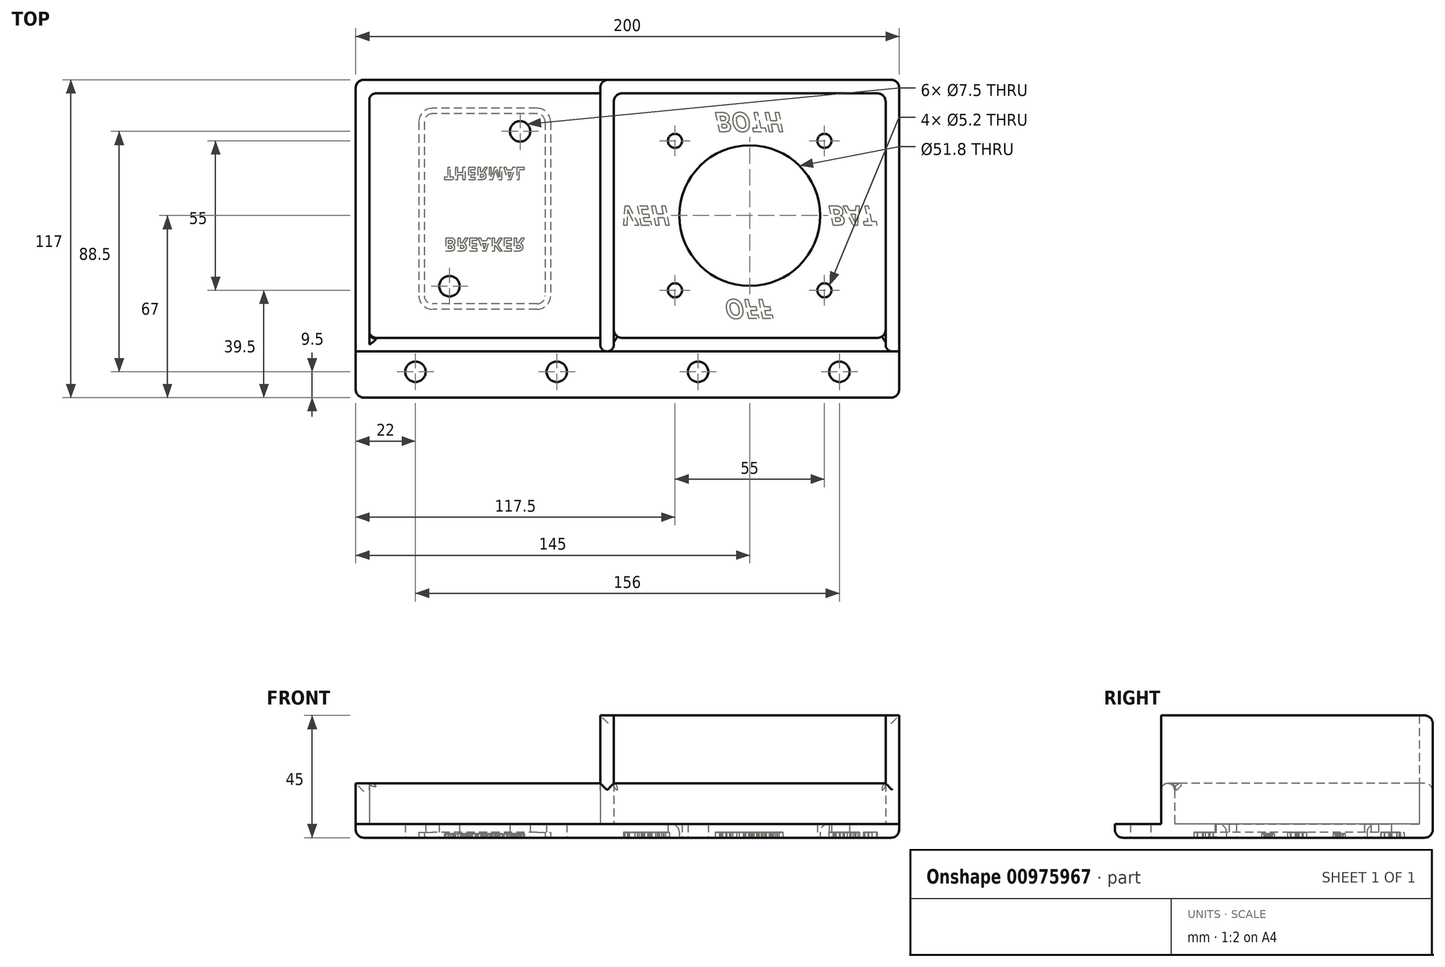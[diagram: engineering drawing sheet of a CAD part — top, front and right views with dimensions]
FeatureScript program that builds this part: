
annotation { "Feature Type Name" : "Feature", "Feature Type Description" : "" }
export const myFeature = defineFeature(function(context is Context, id is Id, definition is map)
    precondition{}
    {
        {
            var Q0;
            Q0=qCreatedBy(makeId("Top.planeOp"),FACE);
            var sketch = newSketch(context, id + "F0", { "sketchPlane" : qUnion([Q0])});
            skLineSegment(sketch, "E0.bottom", {"start": v(-55, 50) * mm, "end": v(55, 50) * mm});
            skLineSegment(sketch, "E0.left", {"start": v(-55, 50) * mm, "end": v(-55, -50) * mm});
            skLineSegment(sketch, "E0.right", {"start": v(55, 50) * mm, "end": v(55, -50) * mm});
            skLineSegment(sketch, "E1", {"start": v(-55, 0) * mm, "end": v(55, 0) * mm, "construction": true});
            skPoint(sketch, "E1.endSnap0", {"position": v(55, 0) * mm});
            skCircle(sketch, "E2", {"center": v(0, 0) * mm, "radius": 25.9 * mm});
            skCircle(sketch, "E3", {"center": v(-27.5, 27.5) * mm, "radius": 2.6 * mm});
            skCircle(sketch, "E4.1.0", {"center": v(-27.5, -27.5) * mm, "radius": 2.6 * mm});
            skCircle(sketch, "E4.2.0", {"center": v(27.5, -27.5) * mm, "radius": 2.6 * mm});
            skCircle(sketch, "E4.3.0", {"center": v(27.5, 27.5) * mm, "radius": 2.6 * mm});
            skLineSegment(sketch, "E5.top", {"start": v(-55, -67) * mm, "end": v(55, -67) * mm});
            skLineSegment(sketch, "E5.left", {"start": v(-55, -50) * mm, "end": v(-55, -67) * mm});
            skLineSegment(sketch, "E5.right", {"start": v(55, -50) * mm, "end": v(55, -67) * mm});
            skLineSegment(sketch, "E6", {"start": v(0, 50) * mm, "end": v(0, -67) * mm, "construction": true});
            skLineSegment(sketch, "E7", {"start": v(-55, -50) * mm, "end": v(55, -50) * mm, "construction": true});
            skSolve(sketch);
        }
        {
            var Q0;
            Q0 = qSketchRegion(id + "F0", true);
            extrude(context, id + "F1", {"entities" : qUnion([Q0]), "depth" : 5 * mm, "offsetDistance" : 25 * mm});
        }
        {
            var Q0;
            Q0=makeQuery(id+"F1.opExtrude","CAP_FACE",FACE,{"disambiguationData":[OSD([sQuery(id+"F0.wireOp",EDGE,"E0.bottom"),sQuery(id+"F0.wireOp",EDGE,"E0.left"),sQuery(id+"F0.wireOp",EDGE,"E0.right"),sQuery(id+"F0.wireOp",EDGE,"E2"),sQuery(id+"F0.wireOp",EDGE,"E3"),sQuery(id+"F0.wireOp",EDGE,"E4.1.0"),sQuery(id+"F0.wireOp",EDGE,"E4.2.0"),sQuery(id+"F0.wireOp",EDGE,"E4.3.0"),sQuery(id+"F0.wireOp",EDGE,"E5.top"),sQuery(id+"F0.wireOp",EDGE,"E5.left"),sQuery(id+"F0.wireOp",EDGE,"E5.right")])],"isStart":false});
            var sketch = newSketch(context, id + "F2", { "sketchPlane" : qUnion([Q0])});
            skPoint(sketch, "E8.0", {"position": v(-55, -50) * mm});
            skPoint(sketch, "E8.1", {"position": v(55, -50) * mm});
            skPoint(sketch, "E8.2", {"position": v(55, 50) * mm});
            skPoint(sketch, "E8.3", {"position": v(-55, 50) * mm});
            skLineSegment(sketch, "E9.bottom", {"start": v(-55, -50) * mm, "end": v(55, -50) * mm});
            skLineSegment(sketch, "E9.top", {"start": v(-55, -45) * mm, "end": v(55, -45) * mm});
            skLineSegment(sketch, "E9.left", {"start": v(-55, -50) * mm, "end": v(-55, -45) * mm});
            skLineSegment(sketch, "E9.right", {"start": v(55, -50) * mm, "end": v(55, -45) * mm});
            skSolve(sketch);
        }
        {
            var Q0;
            Q0 = qSketchRegion(id + "F2", true);
            extrude(context, id + "F3", {"entities" : qUnion([Q0]), "operationType" : NewBodyOperationType.ADD, "depth" : 15 * mm, "offsetDistance" : 25 * mm});
        }
        {
            var Q0;
            {var subQ0=sQuery(id+"F0.wireOp",EDGE,"E4.3.0");var subQ1=sQuery(id+"F0.wireOp",EDGE,"E4.2.0");var subQ2=sQuery(id+"F0.wireOp",EDGE,"E4.1.0");var subQ3=sQuery(id+"F0.wireOp",EDGE,"E3");var subQ4=sQuery(id+"F0.wireOp",EDGE,"E0.bottom");var subQ5=sQuery(id+"F0.wireOp",EDGE,"E2");var subQ6=sQuery(id+"F0.wireOp",EDGE,"E5.left");var subQ7=sQuery(id+"F0.wireOp",EDGE,"E0.left");var subQ8=sQuery(id+"F0.wireOp",EDGE,"E5.right");var subQ9=sQuery(id+"F0.wireOp",EDGE,"E0.right");Q0=makeQuery(id+"F3.boolean.opBoolean","SPLIT",FACE,{"disambiguationData":[TD([makeQuery(id+"F1.opExtrude","SWEPT_FACE",FACE,{"disambiguationData":[OSD([subQ4])]})])],"derivedFrom":makeQuery(id+"F1.opExtrude","CAP_FACE",FACE,{"disambiguationData":[OSD([subQ4,subQ7,subQ9,subQ5,subQ3,subQ2,subQ1,subQ0,sQuery(id+"F0.wireOp",EDGE,"E5.top"),subQ6,subQ8])],"isStart":false})});}
            var sketch = newSketch(context, id + "F4", { "sketchPlane" : qUnion([Q0])});
            skPoint(sketch, "E10", {"position": v(-55, -45) * mm});
            skPoint(sketch, "E11", {"position": v(55, -45) * mm});
            skPoint(sketch, "E12", {"position": v(55, 50) * mm});
            skPoint(sketch, "E13", {"position": v(-55, 50) * mm});
            skLineSegment(sketch, "E14", {"start": v(-55, -45) * mm, "end": v(-55, 50) * mm});
            skLineSegment(sketch, "E15", {"start": v(55, 50) * mm, "end": v(55, -45) * mm});
            skLineSegment(sketch, "E16", {"start": v(55, 50) * mm, "end": v(-55, 50) * mm});
            skLineSegment(sketch, "E17.0", {"start": v(-50, 45) * mm, "end": v(-50, -45) * mm});
            skLineSegment(sketch, "E17.1", {"start": v(-50, 45) * mm, "end": v(50, 45) * mm});
            skLineSegment(sketch, "E17.2", {"start": v(50, 45) * mm, "end": v(50, -45) * mm});
            skLineSegment(sketch, "E18.0", {"start": v(-55, -50) * mm, "end": v(55, -50) * mm, "construction": true});
            skLineSegment(sketch, "E19", {"start": v(-50, -45) * mm, "end": v(-50, -50) * mm});
            skLineSegment(sketch, "E20", {"start": v(-50, -50) * mm, "end": v(-55, -50) * mm});
            skLineSegment(sketch, "E21", {"start": v(-55, -45) * mm, "end": v(-55, -50) * mm});
            skLineSegment(sketch, "E22", {"start": v(50, -45) * mm, "end": v(50, -50) * mm});
            skLineSegment(sketch, "E23", {"start": v(50, -50) * mm, "end": v(55, -50) * mm});
            skLineSegment(sketch, "E24", {"start": v(55, -50) * mm, "end": v(55, -45) * mm});
            skSolve(sketch);
        }
        {
            var Q0;
            Q0 = qSketchRegion(id + "F4", true);
            extrude(context, id + "F5", {"entities" : qUnion([Q0]), "operationType" : NewBodyOperationType.ADD, "depth" : 40 * mm, "offsetDistance" : 25 * mm});
        }
        {
            var Q0;
            Q0=makeQuery(id+"F1.opExtrude","CAP_FACE",FACE,{"disambiguationData":[OSD([sQuery(id+"F0.wireOp",EDGE,"E0.bottom"),sQuery(id+"F0.wireOp",EDGE,"E0.left"),sQuery(id+"F0.wireOp",EDGE,"E0.right"),sQuery(id+"F0.wireOp",EDGE,"E2"),sQuery(id+"F0.wireOp",EDGE,"E3"),sQuery(id+"F0.wireOp",EDGE,"E4.1.0"),sQuery(id+"F0.wireOp",EDGE,"E4.2.0"),sQuery(id+"F0.wireOp",EDGE,"E4.3.0"),sQuery(id+"F0.wireOp",EDGE,"E5.top"),sQuery(id+"F0.wireOp",EDGE,"E5.left"),sQuery(id+"F0.wireOp",EDGE,"E5.right"),sQuery(id+"F0.wireOp",EDGE,"ieUNR4w9-COn6-LHzo-3ocg-rUJtnCFGLiek"),sQuery(id+"F0.wireOp",EDGE,"8SAqncMq-VlD1-aBeH-zWrK-STvUGTyLFCcA")])],"isStart":true});
            var sketch = newSketch(context, id + "F6", { "sketchPlane" : qUnion([Q0])});
            skText(sketch, "E25", { "text": "OFF", "fontName": "OpenSans-BoldItalic.ttf"});
            skLineSegment(sketch, "E26", {"start": v(0, -50) * mm, "end": v(0, 67) * mm, "construction": true});
            skLineSegment(sketch, "E27", {"start": v(55, 0) * mm, "end": v(-55, 0) * mm, "construction": true});
            skPoint(sketch, "E28", {"position": v(0, -25.9) * mm});
            skPoint(sketch, "E29", {"position": v(-25.9, 0) * mm});
            skText(sketch, "E30", { "text": "BAT", "fontName": "OpenSans-BoldItalic.ttf"});
            skPoint(sketch, "E31", {"position": v(28.9, 0) * mm});
            skText(sketch, "E32", { "text": "VEH", "fontName": "OpenSans-BoldItalic.ttf"});
            skPoint(sketch, "E33", {"position": v(-28.9, 0) * mm});
            skText(sketch, "E34", { "text": "BOTH", "fontName": "OpenSans-BoldItalic.ttf"});
            const initialGuessF6  = {"E25": [-0.00924, 0.0309, 1, 0, 0.007], "E30": [0.0289, -0.0035, 1, 0, 0.007], "E32": [-0.0474, -0.0035, 1, 0, 0.007], "E34": [-0.01289, -0.0379, 1, 0, 0.007]};
            skSetInitialGuess(sketch, initialGuessF6);
            skSolve(sketch);
        }
        {
            var Q0;
            Q0 = qSketchRegion(id + "F6", true);
            extrude(context, id + "F7", {"entities" : qUnion([Q0]), "operationType" : NewBodyOperationType.REMOVE, "oppositeDirection" : true, "depth" : 2 * mm, "offsetDistance" : 25 * mm});
        }
        {
            var Q0;
            Q0=qCreatedBy(makeId("Top.planeOp"),FACE);
            var sketch = newSketch(context, id + "F8", { "sketchPlane" : qUnion([Q0])});
            skPoint(sketch, "E35.0", {"position": v(-55, -67) * mm});
            skPoint(sketch, "E35.1", {"position": v(-55, 50) * mm});
            skLineSegment(sketch, "E36.bottom", {"start": v(-55, 50) * mm, "end": v(-145, 50) * mm});
            skLineSegment(sketch, "E36.top", {"start": v(-55, -67) * mm, "end": v(-145, -67) * mm});
            skLineSegment(sketch, "E36.left", {"start": v(-55, 50) * mm, "end": v(-55, -67) * mm});
            skLineSegment(sketch, "E36.right", {"start": v(-145, 50) * mm, "end": v(-145, -67) * mm});
            skSolve(sketch);
        }
        {
            var Q0;
            Q0 = qSketchRegion(id + "F8", true);
            extrude(context, id + "F9", {"entities" : qUnion([Q0]), "operationType" : NewBodyOperationType.ADD, "depth" : 5 * mm, "offsetDistance" : 25 * mm});
        }
        {
            var Q0;
            {var subQ0=sQuery(id+"F0.wireOp",EDGE,"ieUNR4w9-COn6-LHzo-3ocg-rUJtnCFGLiek");var subQ1=sQuery(id+"F0.wireOp",EDGE,"E5.top");var subQ2=sQuery(id+"F0.wireOp",EDGE,"E5.right");var subQ3=sQuery(id+"F0.wireOp",EDGE,"E0.right");var subQ4=sQuery(id+"F0.wireOp",EDGE,"E5.left");var subQ5=sQuery(id+"F0.wireOp",EDGE,"E0.left");var subQ6=sQuery(id+"F0.wireOp",EDGE,"8SAqncMq-VlD1-aBeH-zWrK-STvUGTyLFCcA");Q0=makeQuery(id+"F9.boolean.opBoolean","MERGE",FACE,{"derivedFrom":[makeQuery(id+"F3.boolean.opBoolean","SPLIT",FACE,{"disambiguationData":[TD([makeQuery(id+"F1.opExtrude","SWEPT_FACE",FACE,{"disambiguationData":[OSD([subQ1])]})])],"derivedFrom":makeQuery(id+"F1.opExtrude","CAP_FACE",FACE,{"disambiguationData":[OSD([sQuery(id+"F0.wireOp",EDGE,"E0.bottom"),subQ5,subQ3,sQuery(id+"F0.wireOp",EDGE,"E2"),sQuery(id+"F0.wireOp",EDGE,"E3"),sQuery(id+"F0.wireOp",EDGE,"E4.1.0"),sQuery(id+"F0.wireOp",EDGE,"E4.2.0"),sQuery(id+"F0.wireOp",EDGE,"E4.3.0"),subQ1,subQ4,subQ2,subQ0,subQ6])],"isStart":false})}),makeQuery(id+"F9.opExtrude","CAP_FACE",FACE,{"disambiguationData":[OSD([sQuery(id+"F8.wireOp",EDGE,"E36.bottom"),sQuery(id+"F8.wireOp",EDGE,"E36.top"),sQuery(id+"F8.wireOp",EDGE,"E36.left"),sQuery(id+"F8.wireOp",EDGE,"E36.right")])],"isStart":false})]});}
            var sketch = newSketch(context, id + "F10", { "sketchPlane" : qUnion([Q0])});
            skLineSegment(sketch, "E37.bottom", {"start": v(-55, -50) * mm, "end": v(-145, -50) * mm});
            skLineSegment(sketch, "E37.top", {"start": v(-55, -45) * mm, "end": v(-140, -45) * mm});
            skLineSegment(sketch, "E37.left", {"start": v(-55, -50) * mm, "end": v(-55, -45) * mm});
            skLineSegment(sketch, "E37.right", {"start": v(-145, -50) * mm, "end": v(-145, -45) * mm});
            skLineSegment(sketch, "E38.bottom", {"start": v(-145, 50) * mm, "end": v(-140, 50) * mm});
            skLineSegment(sketch, "E38.top", {"start": v(-145, -45) * mm, "end": v(-140, -45) * mm});
            skLineSegment(sketch, "E38.left", {"start": v(-145, 50) * mm, "end": v(-145, -45) * mm});
            skLineSegment(sketch, "E38.right", {"start": v(-140, 45) * mm, "end": v(-140, -45) * mm});
            skLineSegment(sketch, "E39.bottom", {"start": v(-145, 50) * mm, "end": v(-55, 50) * mm});
            skLineSegment(sketch, "E39.top", {"start": v(-140, 45) * mm, "end": v(-55, 45) * mm});
            skLineSegment(sketch, "E39.left", {"start": v(-145, 50) * mm, "end": v(-145, 45) * mm});
            skLineSegment(sketch, "E39.right", {"start": v(-55, 50) * mm, "end": v(-55, 45) * mm});
            skSolve(sketch);
        }
        {
            var Q0;
            Q0 = qSketchRegion(id + "F10", true);
            var Q1;
            Q1=makeQuery(id+"F3.opExtrude","CAP_FACE",FACE,{"disambiguationData":[OSD([sQuery(id+"F2.wireOp",EDGE,"E9.bottom"),sQuery(id+"F2.wireOp",EDGE,"E9.top"),sQuery(id+"F2.wireOp",EDGE,"E9.left"),sQuery(id+"F2.wireOp",EDGE,"E9.right")])],"isStart":false});
            extrude(context, id + "F11", {"entities" : qUnion([Q0]), "operationType" : NewBodyOperationType.ADD, "endBound" : BoundingType.UP_TO_SURFACE, "depth" : 25 * mm, "endBoundEntityFace" : qUnion([Q1]), "offsetDistance" : 25 * mm});
        }
        {
            var Q0;
            {var subQ0=sQuery(id+"F0.wireOp",EDGE,"E5.top");var subQ1=sQuery(id+"F0.wireOp",EDGE,"E4.3.0");var subQ2=sQuery(id+"F0.wireOp",EDGE,"E3");var subQ3=sQuery(id+"F0.wireOp",EDGE,"E2");var subQ4=sQuery(id+"F0.wireOp",EDGE,"E5.right");var subQ5=sQuery(id+"F0.wireOp",EDGE,"E0.right");var subQ6=sQuery(id+"F0.wireOp",EDGE,"E5.left");var subQ7=sQuery(id+"F0.wireOp",EDGE,"E0.left");var subQ8=sQuery(id+"F0.wireOp",EDGE,"E4.2.0");var subQ9=sQuery(id+"F0.wireOp",EDGE,"E4.1.0");var subQ10=sQuery(id+"F0.wireOp",EDGE,"E0.bottom");Q0=makeQuery(id+"F9.boolean.opBoolean","MERGE",FACE,{"derivedFrom":[makeQuery(id+"F7.boolean.opBoolean","SPLIT",FACE,{"disambiguationData":[TD([makeQuery(id+"F1.opExtrude","SWEPT_FACE",FACE,{"disambiguationData":[OSD([subQ10])]})])],"derivedFrom":makeQuery(id+"F1.opExtrude","CAP_FACE",FACE,{"disambiguationData":[OSD([subQ10,subQ7,subQ5,subQ3,subQ2,subQ9,subQ8,subQ1,subQ0,subQ6,subQ4])],"isStart":true})}),makeQuery(id+"F9.opExtrude","CAP_FACE",FACE,{"disambiguationData":[OSD([sQuery(id+"F8.wireOp",EDGE,"E36.bottom"),sQuery(id+"F8.wireOp",EDGE,"E36.top"),sQuery(id+"F8.wireOp",EDGE,"E36.left"),sQuery(id+"F8.wireOp",EDGE,"E36.right")])],"isStart":true})]});}
            var sketch = newSketch(context, id + "F12", { "sketchPlane" : qUnion([Q0])});
            skPoint(sketch, "E40.0", {"position": v(-145, 50) * mm});
            skPoint(sketch, "E40.1", {"position": v(55, 50) * mm});
            skLineSegment(sketch, "E41", {"start": v(55, 50) * mm, "end": v(-145, 50) * mm, "construction": true});
            skCircle(sketch, "E42", {"center": v(33, 57.5) * mm, "radius": 3.75 * mm});
            skCircle(sketch, "E43", {"center": v(-19, 57.5) * mm, "radius": 3.75 * mm});
            skCircle(sketch, "E44", {"center": v(-71, 57.5) * mm, "radius": 3.75 * mm});
            skCircle(sketch, "E45", {"center": v(-123, 57.5) * mm, "radius": 3.75 * mm});
            skLineSegment(sketch, "E46", {"start": v(-45, 67) * mm, "end": v(-45, -50) * mm, "construction": true});
            skSolve(sketch);
        }
        {
            var Q0;
            Q0 = qSketchRegion(id + "F12", true);
            extrude(context, id + "F13", {"entities" : qUnion([Q0]), "operationType" : NewBodyOperationType.REMOVE, "endBound" : BoundingType.THROUGH_ALL, "oppositeDirection" : true, "depth" : 25 * mm, "offsetDistance" : 25 * mm});
        }
        {
            var Q0;
            {var subQ0=sQuery(id+"F0.wireOp",EDGE,"E5.top");var subQ1=sQuery(id+"F0.wireOp",EDGE,"E4.3.0");var subQ2=sQuery(id+"F0.wireOp",EDGE,"E3");var subQ3=sQuery(id+"F0.wireOp",EDGE,"E2");var subQ4=sQuery(id+"F0.wireOp",EDGE,"E5.right");var subQ5=sQuery(id+"F0.wireOp",EDGE,"E0.right");var subQ6=sQuery(id+"F0.wireOp",EDGE,"E5.left");var subQ7=sQuery(id+"F0.wireOp",EDGE,"E0.left");var subQ8=sQuery(id+"F0.wireOp",EDGE,"E4.2.0");var subQ9=sQuery(id+"F0.wireOp",EDGE,"E4.1.0");var subQ10=sQuery(id+"F0.wireOp",EDGE,"E0.bottom");Q0=makeQuery(id+"F9.boolean.opBoolean","MERGE",FACE,{"derivedFrom":[makeQuery(id+"F7.boolean.opBoolean","SPLIT",FACE,{"disambiguationData":[TD([makeQuery(id+"F1.opExtrude","SWEPT_FACE",FACE,{"disambiguationData":[OSD([subQ10])]})])],"derivedFrom":makeQuery(id+"F1.opExtrude","CAP_FACE",FACE,{"disambiguationData":[OSD([subQ10,subQ7,subQ5,subQ3,subQ2,subQ9,subQ8,subQ1,subQ0,subQ6,subQ4])],"isStart":true})}),makeQuery(id+"F9.opExtrude","CAP_FACE",FACE,{"disambiguationData":[OSD([sQuery(id+"F8.wireOp",EDGE,"E36.bottom"),sQuery(id+"F8.wireOp",EDGE,"E36.top"),sQuery(id+"F8.wireOp",EDGE,"E36.left"),sQuery(id+"F8.wireOp",EDGE,"E36.right")])],"isStart":true})]});}
            var sketch = newSketch(context, id + "F14", { "sketchPlane" : qUnion([Q0])});
            skPoint(sketch, "E47.0", {"position": v(-140, 45) * mm});
            skPoint(sketch, "E47.1", {"position": v(-55, 45) * mm});
            skLineSegment(sketch, "E48", {"start": v(-55, 45) * mm, "end": v(-140, 45) * mm, "construction": true});
            skLineSegment(sketch, "E49", {"start": v(-97.5, 45) * mm, "end": v(-97.5, -50) * mm, "construction": true});
            skLineSegment(sketch, "E50", {"start": v(-55, -2.5) * mm, "end": v(-140, -2.5) * mm, "construction": true});
            skPoint(sketch, "E50.startSnap0", {"position": v(-97.5, -2.5) * mm});
            skCircle(sketch, "E51", {"center": v(-84.5, -31) * mm, "radius": 3.75 * mm});
            skCircle(sketch, "E52", {"center": v(-110.5, 26) * mm, "radius": 3.75 * mm});
            skLineSegment(sketch, "E53", {"start": v(-84.5, -31) * mm, "end": v(-84.5, -2.5) * mm, "construction": true});
            skLineSegment(sketch, "E54", {"start": v(-110.5, 26) * mm, "end": v(-110.5, -2.5) * mm, "construction": true});
            skLineSegment(sketch, "E55", {"start": v(-84.5, -31) * mm, "end": v(-97.5, -31) * mm});
            skLineSegment(sketch, "E56", {"start": v(-110.5, 26) * mm, "end": v(-97.5, 26) * mm});
            skSolve(sketch);
        }
        {
            var Q0;
            Q0 = qSketchRegion(id + "F14", true);
            extrude(context, id + "F15", {"entities" : qUnion([Q0]), "operationType" : NewBodyOperationType.REMOVE, "endBound" : BoundingType.THROUGH_ALL, "oppositeDirection" : true, "depth" : 25 * mm, "offsetDistance" : 25 * mm});
        }
        {
            var Q0;
            {var subQ0=sQuery(id+"F0.wireOp",EDGE,"E5.top");var subQ1=sQuery(id+"F0.wireOp",EDGE,"E4.3.0");var subQ2=sQuery(id+"F0.wireOp",EDGE,"E3");var subQ3=sQuery(id+"F0.wireOp",EDGE,"E2");var subQ4=sQuery(id+"F0.wireOp",EDGE,"E5.right");var subQ5=sQuery(id+"F0.wireOp",EDGE,"E0.right");var subQ6=sQuery(id+"F0.wireOp",EDGE,"E5.left");var subQ7=sQuery(id+"F0.wireOp",EDGE,"E0.left");var subQ8=sQuery(id+"F0.wireOp",EDGE,"E4.2.0");var subQ9=sQuery(id+"F0.wireOp",EDGE,"E4.1.0");var subQ10=sQuery(id+"F0.wireOp",EDGE,"E0.bottom");Q0=makeQuery(id+"F9.boolean.opBoolean","MERGE",FACE,{"derivedFrom":[makeQuery(id+"F7.boolean.opBoolean","SPLIT",FACE,{"disambiguationData":[TD([makeQuery(id+"F1.opExtrude","SWEPT_FACE",FACE,{"disambiguationData":[OSD([subQ10])]})])],"derivedFrom":makeQuery(id+"F1.opExtrude","CAP_FACE",FACE,{"disambiguationData":[OSD([subQ10,subQ7,subQ5,subQ3,subQ2,subQ9,subQ8,subQ1,subQ0,subQ6,subQ4])],"isStart":true})}),makeQuery(id+"F9.opExtrude","CAP_FACE",FACE,{"disambiguationData":[OSD([sQuery(id+"F8.wireOp",EDGE,"E36.bottom"),sQuery(id+"F8.wireOp",EDGE,"E36.top"),sQuery(id+"F8.wireOp",EDGE,"E36.left"),sQuery(id+"F8.wireOp",EDGE,"E36.right")])],"isStart":true})]});}
            var sketch = newSketch(context, id + "F16", { "sketchPlane" : qUnion([Q0])});
            skLineSegment(sketch, "E57.0", {"start": v(-55, -2.5) * mm, "end": v(-140, -2.5) * mm, "construction": true});
            skLineSegment(sketch, "E57.1", {"start": v(-97.5, 45) * mm, "end": v(-97.5, -50) * mm, "construction": true});
            skLineSegment(sketch, "E58.bottom", {"start": v(-78.25, -39.5) * mm, "end": v(-116.75, -39.5) * mm});
            skLineSegment(sketch, "E58.top", {"start": v(-78.25, 34.5) * mm, "end": v(-116.75, 34.5) * mm});
            skLineSegment(sketch, "E58.left", {"start": v(-73.25, -34.5) * mm, "end": v(-73.25, 29.5) * mm});
            skLineSegment(sketch, "E58.right", {"start": v(-121.75, -34.5) * mm, "end": v(-121.75, 29.5) * mm});
            skPoint(sketch, "E59.visualSharp", {"position": v(-73.25, -39.5) * mm});
            skArc(sketch, "E59.filletArc", {"start": v(-78.25, -39.5) * mm, "mid": v(-74.71, -38.04) * mm, "end": v(-73.25, -34.5) * mm});
            skPoint(sketch, "E60.visualSharp", {"position": v(-121.75, -39.5) * mm});
            skArc(sketch, "E60.filletArc", {"start": v(-121.75, -34.5) * mm, "mid": v(-120.29, -38.04) * mm, "end": v(-116.75, -39.5) * mm});
            skPoint(sketch, "E61.visualSharp", {"position": v(-121.75, 34.5) * mm});
            skArc(sketch, "E61.filletArc", {"start": v(-116.75, 34.5) * mm, "mid": v(-120.29, 33.04) * mm, "end": v(-121.75, 29.5) * mm});
            skPoint(sketch, "E62.visualSharp", {"position": v(-73.25, 34.5) * mm});
            skArc(sketch, "E62.filletArc", {"start": v(-73.25, 29.5) * mm, "mid": v(-74.71, 33.04) * mm, "end": v(-78.25, 34.5) * mm});
            skLineSegment(sketch, "E63.0", {"start": v(-78.25, -37.5) * mm, "end": v(-116.75, -37.5) * mm});
            skArc(sketch, "E63.1", {"start": v(-119.75, -34.5) * mm, "mid": v(-118.87, -36.62) * mm, "end": v(-116.75, -37.5) * mm});
            skArc(sketch, "E63.2", {"start": v(-78.25, -37.5) * mm, "mid": v(-76.13, -36.62) * mm, "end": v(-75.25, -34.5) * mm});
            skLineSegment(sketch, "E63.3", {"start": v(-119.75, -34.5) * mm, "end": v(-119.75, 29.5) * mm});
            skLineSegment(sketch, "E63.4", {"start": v(-75.25, -34.5) * mm, "end": v(-75.25, 29.5) * mm});
            skArc(sketch, "E63.5", {"start": v(-75.25, 29.5) * mm, "mid": v(-76.13, 31.62) * mm, "end": v(-78.25, 32.5) * mm});
            skLineSegment(sketch, "E63.6", {"start": v(-78.25, 32.5) * mm, "end": v(-116.75, 32.5) * mm});
            skArc(sketch, "E63.7", {"start": v(-116.75, 32.5) * mm, "mid": v(-118.87, 31.62) * mm, "end": v(-119.75, 29.5) * mm});
            skSolve(sketch);
        }
        {
            var Q0;
            Q0 = qSketchRegion(id + "F16", true);
            extrude(context, id + "F17", {"entities" : qUnion([Q0]), "operationType" : NewBodyOperationType.REMOVE, "oppositeDirection" : true, "depth" : 2 * mm, "offsetDistance" : 25 * mm});
        }
        {
            var Q0;
            {var subQ0=sQuery(id+"F0.wireOp",EDGE,"E5.top");var subQ1=sQuery(id+"F0.wireOp",EDGE,"E4.3.0");var subQ2=sQuery(id+"F0.wireOp",EDGE,"E3");var subQ3=sQuery(id+"F0.wireOp",EDGE,"E2");var subQ4=sQuery(id+"F0.wireOp",EDGE,"E5.right");var subQ5=sQuery(id+"F0.wireOp",EDGE,"E0.right");var subQ6=sQuery(id+"F0.wireOp",EDGE,"E5.left");var subQ7=sQuery(id+"F0.wireOp",EDGE,"E0.left");var subQ8=sQuery(id+"F0.wireOp",EDGE,"E4.2.0");var subQ9=sQuery(id+"F0.wireOp",EDGE,"E4.1.0");var subQ10=sQuery(id+"F0.wireOp",EDGE,"E0.bottom");Q0=makeQuery(id+"F17.boolean.opBoolean","SPLIT",FACE,{"disambiguationData":[TD([makeQuery(id+"F15.boolean.opBoolean","COPY",FACE,{"derivedFrom":makeQuery(id+"F15.opExtrude","SWEPT_FACE",FACE,{"disambiguationData":[OSD([sQuery(id+"F14.wireOp",EDGE,"E51")])]})})])],"derivedFrom":makeQuery(id+"F9.boolean.opBoolean","MERGE",FACE,{"derivedFrom":[makeQuery(id+"F7.boolean.opBoolean","SPLIT",FACE,{"disambiguationData":[TD([makeQuery(id+"F1.opExtrude","SWEPT_FACE",FACE,{"disambiguationData":[OSD([subQ10])]})])],"derivedFrom":makeQuery(id+"F1.opExtrude","CAP_FACE",FACE,{"disambiguationData":[OSD([subQ10,subQ7,subQ5,subQ3,subQ2,subQ9,subQ8,subQ1,subQ0,subQ6,subQ4])],"isStart":true})}),makeQuery(id+"F9.opExtrude","CAP_FACE",FACE,{"disambiguationData":[OSD([sQuery(id+"F8.wireOp",EDGE,"E36.bottom"),sQuery(id+"F8.wireOp",EDGE,"E36.top"),sQuery(id+"F8.wireOp",EDGE,"E36.left"),sQuery(id+"F8.wireOp",EDGE,"E36.right")])],"isStart":true})]})});}
            var sketch = newSketch(context, id + "F18", { "sketchPlane" : qUnion([Q0])});
            skLineSegment(sketch, "E64", {"start": v(-75.25, -2.5) * mm, "end": v(-119.75, -2.5) * mm, "construction": true});
            skLineSegment(sketch, "E65", {"start": v(-97.5, -37.5) * mm, "end": v(-97.5, 32.5) * mm, "construction": true});
            skText(sketch, "E66", { "text": "THERMAL", "fontName": "OpenSans-Bold.ttf"});
            skText(sketch, "E67", { "text": "BREAKER", "fontName": "OpenSans-Bold.ttf"});
            const initialGuessF18  = {"E66": [-0.1125, -0.01777, 1, 0, 0.0045], "E67": [-0.1125, 0.00826, 1, 0, 0.00477]};
            skSetInitialGuess(sketch, initialGuessF18);
            skSolve(sketch);
        }
        {
            var Q0;
            Q0 = qSketchRegion(id + "F18", true);
            extrude(context, id + "F19", {"entities" : qUnion([Q0]), "operationType" : NewBodyOperationType.REMOVE, "oppositeDirection" : true, "depth" : 1.5 * mm, "offsetDistance" : 25 * mm});
        }
        {
            var Q0;
            Q0=makeQuery(id+"F1.opExtrude","CAP_EDGE",EDGE,{"disambiguationData":[OSD([sQuery(id+"F0.wireOp",EDGE,"E0.left"),sQuery(id+"F0.wireOp",EDGE,"E5.left")])],"isStart":true});
            var Q1;
            Q1=makeQuery(id+"F1.opExtrude","CAP_EDGE",EDGE,{"disambiguationData":[OSD([sQuery(id+"F0.wireOp",EDGE,"E0.bottom")])],"isStart":true});
            var Q2;
            Q2=makeQuery(id+"F1.opExtrude","CAP_EDGE",EDGE,{"disambiguationData":[OSD([sQuery(id+"F0.wireOp",EDGE,"E0.right"),sQuery(id+"F0.wireOp",EDGE,"E5.right")])],"isStart":true});
            var Q3;
            Q3=makeQuery(id+"F1.opExtrude","CAP_EDGE",EDGE,{"disambiguationData":[OSD([sQuery(id+"F0.wireOp",EDGE,"E5.top")])],"isStart":true});
            var Q4;
            Q4=makeQuery(id+"F5.boolean.opBoolean","MERGE",EDGE,{"derivedFrom":[makeQuery(id+"F1.opExtrude","SWEPT_EDGE",EDGE,{"disambiguationData":[OSD([sQuery(id+"F0.wireOp",EDGE,"E0.bottom"),sQuery(id+"F0.wireOp",EDGE,"E0.left")])]}),makeQuery(id+"F5.opExtrude","SWEPT_EDGE",EDGE,{"disambiguationData":[OSD([sQuery(id+"F4.wireOp",EDGE,"E14"),sQuery(id+"F4.wireOp",EDGE,"E16")])]})]});
            var Q5;
            Q5=makeQuery(id+"F5.boolean.opBoolean","MERGE",EDGE,{"derivedFrom":[makeQuery(id+"F1.opExtrude","SWEPT_EDGE",EDGE,{"disambiguationData":[OSD([sQuery(id+"F0.wireOp",EDGE,"E0.bottom"),sQuery(id+"F0.wireOp",EDGE,"E0.right")])]}),makeQuery(id+"F5.opExtrude","SWEPT_EDGE",EDGE,{"disambiguationData":[OSD([sQuery(id+"F4.wireOp",EDGE,"E15"),sQuery(id+"F4.wireOp",EDGE,"E16")])]})]});
            var Q6;
            Q6=makeQuery(id+"F1.opExtrude","SWEPT_EDGE",EDGE,{"disambiguationData":[OSD([sQuery(id+"F0.wireOp",EDGE,"E5.top"),sQuery(id+"F0.wireOp",EDGE,"E5.right")])]});
            var Q7;
            Q7=makeQuery(id+"F1.opExtrude","SWEPT_EDGE",EDGE,{"disambiguationData":[OSD([sQuery(id+"F0.wireOp",EDGE,"E5.top"),sQuery(id+"F0.wireOp",EDGE,"E5.left")])]});
            var Q8;
            Q8=makeQuery(id+"F9.opExtrude","CAP_EDGE",EDGE,{"disambiguationData":[OSD([sQuery(id+"F8.wireOp",EDGE,"E36.right")])],"isStart":true});
            var Q9;
            Q9=makeQuery(id+"F11.boolean.opBoolean","MERGE",EDGE,{"derivedFrom":[makeQuery(id+"F9.opExtrude","SWEPT_EDGE",EDGE,{"disambiguationData":[OSD([sQuery(id+"F8.wireOp",EDGE,"E36.bottom"),sQuery(id+"F8.wireOp",EDGE,"E36.right")])]}),makeQuery(id+"F11.opExtrude","SWEPT_EDGE",EDGE,{"disambiguationData":[OSD([sQuery(id+"F10.wireOp",EDGE,"E39.bottom"),sQuery(id+"F10.wireOp",EDGE,"E39.left")])]})]});
            var Q10;
            Q10=makeQuery(id+"F9.opExtrude","SWEPT_EDGE",EDGE,{"disambiguationData":[OSD([sQuery(id+"F8.wireOp",EDGE,"E36.top"),sQuery(id+"F8.wireOp",EDGE,"E36.right")])]});
            var Q11;
            Q11=makeQuery(id+"F11.opExtrude","CAP_EDGE",EDGE,{"disambiguationData":[OSD([sQuery(id+"F10.wireOp",EDGE,"E39.bottom")])],"isStart":false});
            var Q12;
            Q12=makeQuery(id+"F5.opExtrude","CAP_EDGE",EDGE,{"disambiguationData":[OSD([sQuery(id+"F4.wireOp",EDGE,"E16")])],"isStart":false});
            fillet(context, id + "F20", {"entities" : qUnion([Q0, Q1, Q2, Q3, Q4, Q5, Q6, Q7, Q8, Q9, Q10, Q11, Q12]), "radius" : 3 * mm, "tangentPropagation" : true, "allowEdgeOverflow" : false});
        }
        {
            var Q0;
            Q0=makeQuery(id+"F1.opExtrude","CAP_EDGE",EDGE,{"disambiguationData":[OSD([sQuery(id+"F0.wireOp",EDGE,"E2")])],"isStart":false});
            fillet(context, id + "F21", {"entities" : qUnion([Q0]), "radius" : 3 * mm, "tangentPropagation" : true, "allowEdgeOverflow" : false});
        }
        {
            var Q0;
            Q0=makeQuery(id+"F5.opExtrude","CAP_EDGE",EDGE,{"disambiguationData":[OSD([sQuery(id+"F4.wireOp",EDGE,"E17.0"),sQuery(id+"F4.wireOp",EDGE,"E19")])],"isStart":true});
            var Q1;
            Q1=makeQuery(id+"F3.opExtrude","CAP_EDGE",EDGE,{"disambiguationData":[OSD([sQuery(id+"F2.wireOp",EDGE,"E9.top")])],"isStart":true});
            var Q2;
            Q2=makeQuery(id+"F5.opExtrude","CAP_EDGE",EDGE,{"disambiguationData":[OSD([sQuery(id+"F4.wireOp",EDGE,"E17.2"),sQuery(id+"F4.wireOp",EDGE,"E22")])],"isStart":true});
            var Q3;
            Q3=makeQuery(id+"F5.opExtrude","CAP_EDGE",EDGE,{"disambiguationData":[OSD([sQuery(id+"F4.wireOp",EDGE,"E17.1")])],"isStart":true});
            var Q4;
            Q4=makeQuery(id+"F5.opExtrude","SWEPT_EDGE",EDGE,{"disambiguationData":[OSD([sQuery(id+"F4.wireOp",EDGE,"E17.0"),sQuery(id+"F4.wireOp",EDGE,"E17.1")])]});
            var Q5;
            Q5=makeQuery(id+"F5.opExtrude","SWEPT_EDGE",EDGE,{"disambiguationData":[OSD([sQuery(id+"F4.wireOp",EDGE,"E17.1"),sQuery(id+"F4.wireOp",EDGE,"E17.2")])]});
            var Q6;
            Q6=makeQuery(id+"F5.boolean.opBoolean","INTERSECT",EDGE,{"derivedFrom":[makeQuery(id+"F3.opExtrude","SWEPT_FACE",FACE,{"disambiguationData":[OSD([sQuery(id+"F2.wireOp",EDGE,"E9.top")])]}),makeQuery(id+"F5.opExtrude","SWEPT_FACE",FACE,{"disambiguationData":[OSD([sQuery(id+"F4.wireOp",EDGE,"E17.2"),sQuery(id+"F4.wireOp",EDGE,"E22")])]})]});
            var Q7;
            Q7=makeQuery(id+"F5.boolean.opBoolean","INTERSECT",EDGE,{"derivedFrom":[makeQuery(id+"F3.opExtrude","SWEPT_FACE",FACE,{"disambiguationData":[OSD([sQuery(id+"F2.wireOp",EDGE,"E9.top")])]}),makeQuery(id+"F5.opExtrude","SWEPT_FACE",FACE,{"disambiguationData":[OSD([sQuery(id+"F4.wireOp",EDGE,"E17.0"),sQuery(id+"F4.wireOp",EDGE,"E19")])]})]});
            fillet(context, id + "F22", {"entities" : qUnion([Q0, Q1, Q2, Q3, Q4, Q5, Q6, Q7]), "radius" : 3 * mm, "tangentPropagation" : true, "allowEdgeOverflow" : false});
        }
        {
            var Q0;
            Q0=makeQuery(id+"F3.opExtrude","CAP_EDGE",EDGE,{"disambiguationData":[OSD([sQuery(id+"F2.wireOp",EDGE,"E9.top")])],"isStart":false});
            var Q1;
            Q1=makeQuery(id+"F3.opExtrude","CAP_EDGE",EDGE,{"disambiguationData":[OSD([sQuery(id+"F2.wireOp",EDGE,"E9.bottom")])],"isStart":false});
            var Q2;
            Q2=makeQuery(id+"F5.opExtrude","SWEPT_EDGE",EDGE,{"disambiguationData":[OSD([sQuery(id+"F4.wireOp",EDGE,"E19"),sQuery(id+"F4.wireOp",EDGE,"E20")])]});
            var Q3;
            Q3=makeQuery(id+"F5.opExtrude","SWEPT_EDGE",EDGE,{"disambiguationData":[OSD([sQuery(id+"F4.wireOp",EDGE,"E22"),sQuery(id+"F4.wireOp",EDGE,"E23")])]});
            var Q4;
            Q4=makeQuery(id+"F11.opExtrude","CAP_EDGE",EDGE,{"disambiguationData":[OSD([sQuery(id+"F10.wireOp",EDGE,"E37.bottom")])],"isStart":false});
            var Q5;
            Q5=makeQuery(id+"F11.opExtrude","CAP_EDGE",EDGE,{"disambiguationData":[OSD([sQuery(id+"F10.wireOp",EDGE,"E37.top")])],"isStart":false});
            var Q6;
            Q6=makeQuery(id+"F11.opExtrude","CAP_EDGE",EDGE,{"disambiguationData":[OSD([sQuery(id+"F10.wireOp",EDGE,"E37.top")])],"isStart":true});
            var Q7;
            Q7=makeQuery(id+"F11.opExtrude","CAP_EDGE",EDGE,{"disambiguationData":[OSD([sQuery(id+"F10.wireOp",EDGE,"E38.right")])],"isStart":true});
            var Q8;
            Q8=makeQuery(id+"F9.opExtrude","CAP_EDGE",EDGE,{"disambiguationData":[OSD([sQuery(id+"F8.wireOp",EDGE,"E36.left")])],"isStart":false});
            var Q9;
            Q9=makeQuery(id+"F11.opExtrude","SWEPT_EDGE",EDGE,{"disambiguationData":[OSD([sQuery(id+"F8.wireOp",EDGE,"E36.left"),sQuery(id+"F10.wireOp",EDGE,"E39.top"),sQuery(id+"F10.wireOp",EDGE,"E39.right")])]});
            var Q10;
            Q10=makeQuery(id+"F11.opExtrude","CAP_EDGE",EDGE,{"disambiguationData":[OSD([sQuery(id+"F10.wireOp",EDGE,"E39.top")])],"isStart":true});
            var Q11;
            Q11=makeQuery(id+"F11.opExtrude","SWEPT_EDGE",EDGE,{"disambiguationData":[OSD([sQuery(id+"F10.wireOp",EDGE,"E38.right"),sQuery(id+"F10.wireOp",EDGE,"E39.top")])]});
            var Q12;
            Q12=makeQuery(id+"F5.boolean.opBoolean","MERGE",EDGE,{"derivedFrom":[makeQuery(id+"F3.opExtrude","SWEPT_EDGE",EDGE,{"disambiguationData":[OSD([sQuery(id+"F0.wireOp",EDGE,"E0.left"),sQuery(id+"F0.wireOp",EDGE,"E5.left"),sQuery(id+"F2.wireOp",EDGE,"E9.bottom"),sQuery(id+"F2.wireOp",EDGE,"E9.left")])]}),makeQuery(id+"F5.opExtrude","SWEPT_EDGE",EDGE,{"disambiguationData":[OSD([sQuery(id+"F4.wireOp",EDGE,"E20"),sQuery(id+"F4.wireOp",EDGE,"E21")])]})]});
            fillet(context, id + "F23", {"entities" : qUnion([Q0, Q1, Q2, Q3, Q4, Q5, Q6, Q7, Q8, Q9, Q10, Q11, Q12]), "radius" : 2.5 * mm, "tangentPropagation" : true, "allowEdgeOverflow" : false});
        }
        {
            var Q0;
            Q0=makeQuery(id+"F11.opExtrude","SWEPT_EDGE",EDGE,{"disambiguationData":[OSD([sQuery(id+"F10.wireOp",EDGE,"E37.top"),sQuery(id+"F10.wireOp",EDGE,"E38.top"),sQuery(id+"F10.wireOp",EDGE,"E38.right")])]});
            var Q1;
            Q1=makeQuery(id+"F11.opExtrude","SWEPT_EDGE",EDGE,{"disambiguationData":[OSD([sQuery(id+"F8.wireOp",EDGE,"E36.left"),sQuery(id+"F10.wireOp",EDGE,"E37.top"),sQuery(id+"F10.wireOp",EDGE,"E37.left")])]});
            fillet(context, id + "F24", {"entities" : qUnion([Q0, Q1]), "radius" : 2.5 * mm, "tangentPropagation" : true, "allowEdgeOverflow" : false});
        }
    });
